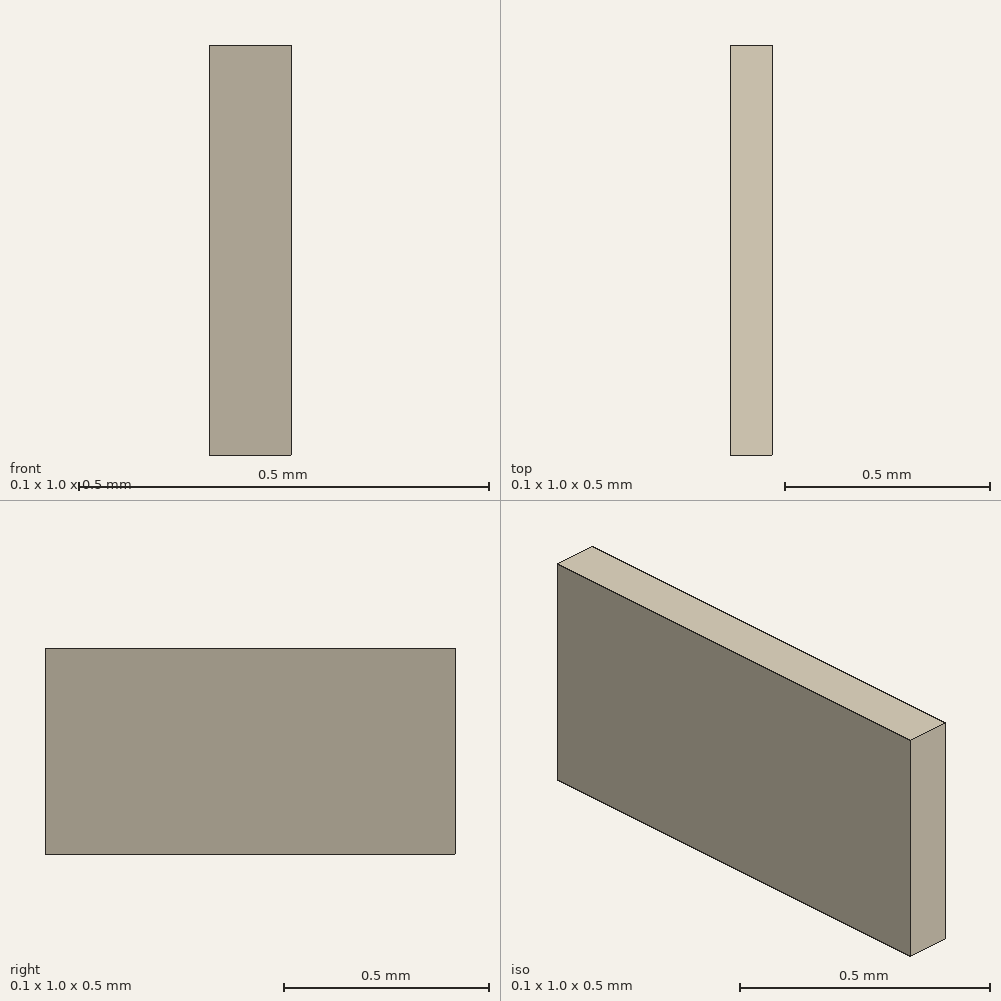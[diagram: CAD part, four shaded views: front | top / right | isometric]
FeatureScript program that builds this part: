
annotation { "Feature Type Name" : "Feature", "Feature Type Description" : "" }
export const myFeature = defineFeature(function(context is Context, id is Id, definition is map)
    precondition{}
    {
        {
            var Q0;
            Q0=qCreatedBy(makeId("Top.planeOp"),FACE);
            var sketch = newSketch(context, id + "F0", { "sketchPlane" : qUnion([Q0])});
            skLineSegment(sketch, "E0", {"start": v(0, 0.5) * mm, "end": v(-0.05, 0.5) * mm});
            skLineSegment(sketch, "E1", {"start": v(-0.05, 0.5) * mm, "end": v(-0.05, -0.5) * mm});
            skLineSegment(sketch, "E2", {"start": v(-0.05, -0.5) * mm, "end": v(0, -0.5) * mm});
            skLineSegment(sketch, "E3.MirrorCS", {"start": v(0.05, -0.5) * mm, "end": v(0, -0.5) * mm});
            skLineSegment(sketch, "E4.MirrorCS", {"start": v(0.05, 0.5) * mm, "end": v(0.05, -0.5) * mm});
            skLineSegment(sketch, "E5.MirrorCS", {"start": v(0, 0.5) * mm, "end": v(0.05, 0.5) * mm});
            skSolve(sketch);
        }
        {
            var Q0;
            Q0 = qSketchRegion(id + "F0", true);
            extrude(context, id + "F1", {"entities" : qUnion([Q0]), "depth" : 0.5 * mm, "offsetDistance" : 25 * mm});
        }
    });
